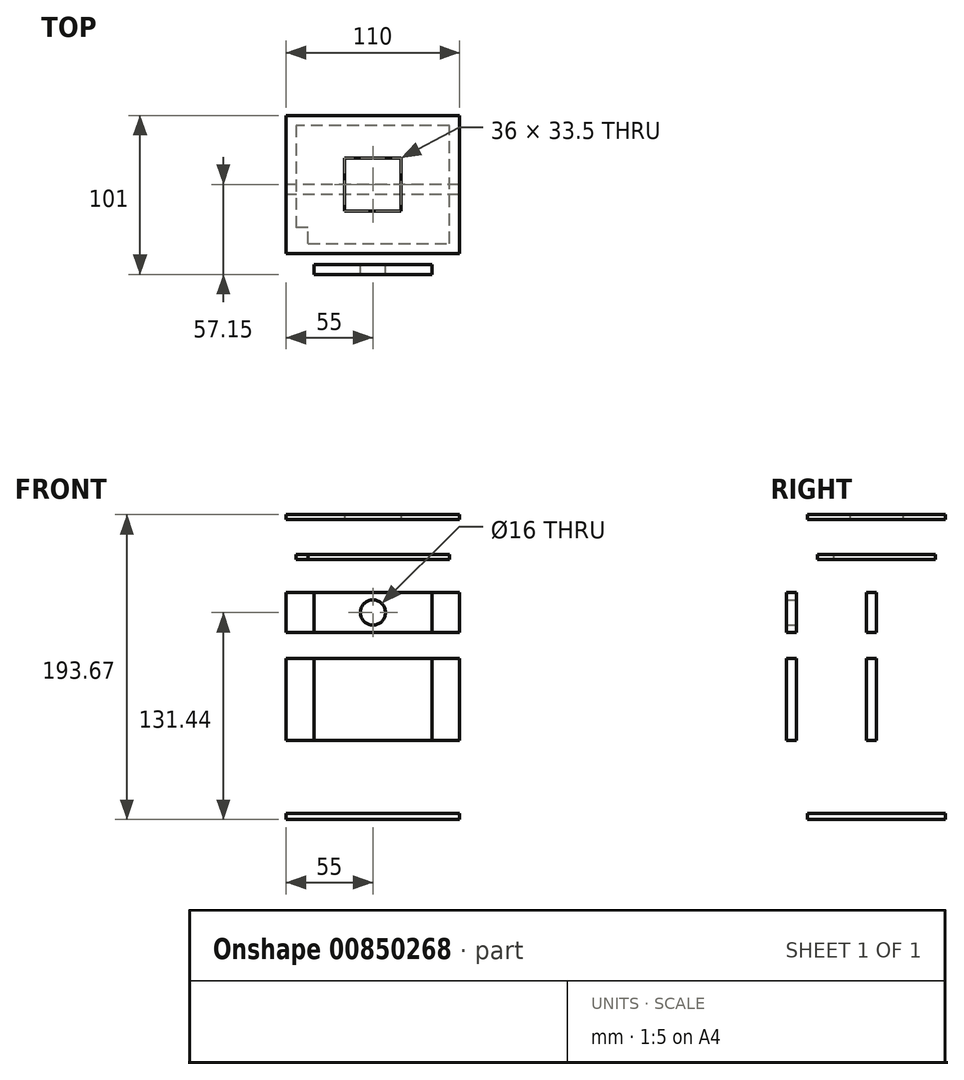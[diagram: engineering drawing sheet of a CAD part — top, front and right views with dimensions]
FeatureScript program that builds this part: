
annotation { "Feature Type Name" : "Feature", "Feature Type Description" : "" }
export const myFeature = defineFeature(function(context is Context, id is Id, definition is map)
    precondition{}
    {
        {
            var Q0;
            Q0=qCreatedBy(makeId("Front.planeOp"),FACE);
            var sketch = newSketch(context, id + "F0", { "sketchPlane" : qUnion([Q0])});
            skLineSegment(sketch, "E0.bottom", {"start": v(55, 26) * mm, "end": v(-55, 26) * mm});
            skLineSegment(sketch, "E0.top", {"start": v(55, -26) * mm, "end": v(-55, -26) * mm});
            skLineSegment(sketch, "E0.left", {"start": v(55, 26) * mm, "end": v(55, -26) * mm});
            skLineSegment(sketch, "E0.right", {"start": v(-55, 26) * mm, "end": v(-55, -26) * mm});
            skPoint(sketch, "E0.middle", {"position": v(0, 0) * mm});
            skSolve(sketch);
        }
        {
            var Q0;
            Q0=makeQuery(id+"F0.imprint","IMPRINT",FACE,{"disambiguationData":[TD([[makeQuery(id+"F0.imprint","IMPRINT",EDGE,{"derivedFrom":sQuery(id+"F0.wireOp",EDGE,"E0.bottom")}),1.0]])]});
            extrude(context, id + "F1", {"entities" : qUnion([Q0]), "depth" : 6.35 * mm, "offsetDistance" : 25.4 * mm});
        }
        {
            var Q0;
            Q0=qCreatedBy(makeId("Front.planeOp"),FACE);
            cPlane(context, id + "F2", {"entities" : qUnion([Q0]), "cplaneType" : CPlaneType.OFFSET, "offset" : 50.8 * mm, "width" : 152.4 * mm, "height" : 152.4 * mm});
        }
        {
            var Q0;
            Q0=qCreatedBy(id+"F2.planeOp",FACE);
            var sketch = newSketch(context, id + "F3", { "sketchPlane" : qUnion([Q0])});
            skLineSegment(sketch, "E1.bottom", {"start": v(37.5, 26) * mm, "end": v(-37.5, 26) * mm});
            skLineSegment(sketch, "E1.top", {"start": v(37.5, -26) * mm, "end": v(-37.5, -26) * mm});
            skLineSegment(sketch, "E1.left", {"start": v(37.5, 26) * mm, "end": v(37.5, -26) * mm});
            skLineSegment(sketch, "E1.right", {"start": v(-37.5, 26) * mm, "end": v(-37.5, -26) * mm});
            skPoint(sketch, "E1.middle", {"position": v(0, 0) * mm});
            skSolve(sketch);
        }
        {
            var Q0;
            Q0=makeQuery(id+"F3.imprint","IMPRINT",FACE,{"disambiguationData":[TD([[makeQuery(id+"F3.imprint","IMPRINT",EDGE,{"derivedFrom":sQuery(id+"F3.wireOp",EDGE,"E1.bottom")}),1.0]])]});
            extrude(context, id + "F4", {"entities" : qUnion([Q0]), "depth" : 6.35 * mm, "offsetDistance" : 25.4 * mm});
        }
        {
            var Q0;
            Q0=qCreatedBy(makeId("Top.planeOp"),FACE);
            cPlane(context, id + "F5", {"entities" : qUnion([Q0]), "cplaneType" : CPlaneType.OFFSET, "offset" : 76.2 * mm, "oppositeDirection" : true, "width" : 152.4 * mm, "height" : 152.4 * mm});
        }
        {
            var Q0;
            Q0=qCreatedBy(id+"F5.planeOp",FACE);
            var sketch = newSketch(context, id + "F6", { "sketchPlane" : qUnion([Q0])});
            skLineSegment(sketch, "E2.bottom", {"start": v(55, 43.85) * mm, "end": v(-55, 43.85) * mm});
            skLineSegment(sketch, "E2.top", {"start": v(55, -43.85) * mm, "end": v(-55, -43.85) * mm});
            skLineSegment(sketch, "E2.left", {"start": v(55, 43.85) * mm, "end": v(55, -43.85) * mm});
            skLineSegment(sketch, "E2.right", {"start": v(-55, 43.85) * mm, "end": v(-55, -43.85) * mm});
            skPoint(sketch, "E2.middle", {"position": v(0, 0) * mm});
            skSolve(sketch);
        }
        {
            var Q0;
            Q0=makeQuery(id+"F6.imprint","IMPRINT",FACE,{"disambiguationData":[TD([[makeQuery(id+"F6.imprint","IMPRINT",EDGE,{"derivedFrom":sQuery(id+"F6.wireOp",EDGE,"E2.bottom")}),1.0]])]});
            extrude(context, id + "F7", {"entities" : qUnion([Q0]), "depth" : 4 * mm, "offsetDistance" : 25.4 * mm});
        }
        {
            var Q0;
            Q0=qCreatedBy(makeId("Front.planeOp"),FACE);
            var sketch = newSketch(context, id + "F8", { "sketchPlane" : qUnion([Q0])});
            skLineSegment(sketch, "E3.bottom", {"start": v(55, 67.94) * mm, "end": v(-55, 67.94) * mm});
            skLineSegment(sketch, "E3.top", {"start": v(55, 42.54) * mm, "end": v(-55, 42.54) * mm});
            skLineSegment(sketch, "E3.left", {"start": v(55, 67.94) * mm, "end": v(55, 42.54) * mm});
            skLineSegment(sketch, "E3.right", {"start": v(-55, 67.94) * mm, "end": v(-55, 42.54) * mm});
            skPoint(sketch, "E3.middle", {"position": v(0, 55.24) * mm});
            skLineSegment(sketch, "E4.0.0", {"start": v(-55, -26) * mm, "end": v(55, -26) * mm});
            skLineSegment(sketch, "E4.0.1", {"start": v(55, -26) * mm, "end": v(55, 26) * mm});
            skLineSegment(sketch, "E4.0.2", {"start": v(55, 26) * mm, "end": v(-55, 26) * mm});
            skLineSegment(sketch, "E4.0.3", {"start": v(-55, 26) * mm, "end": v(-55, -26) * mm});
            skSolve(sketch);
        }
        {
            var Q0;
            Q0=makeQuery(id+"F8.imprint","IMPRINT",FACE,{"disambiguationData":[TD([[makeQuery(id+"F8.imprint","IMPRINT",EDGE,{"derivedFrom":sQuery(id+"F8.wireOp",EDGE,"E3.bottom")}),1.0]])]});
            extrude(context, id + "F9", {"entities" : qUnion([Q0]), "depth" : 6.35 * mm, "offsetDistance" : 25.4 * mm});
        }
        {
            var Q0;
            Q0=qCreatedBy(id+"F2.planeOp",FACE);
            var sketch = newSketch(context, id + "F10", { "sketchPlane" : qUnion([Q0])});
            skLineSegment(sketch, "E5.0.0", {"start": v(-37.5, -26) * mm, "end": v(37.5, -26) * mm});
            skLineSegment(sketch, "E5.0.1", {"start": v(37.5, -26) * mm, "end": v(37.5, 26) * mm});
            skLineSegment(sketch, "E5.0.2", {"start": v(37.5, 26) * mm, "end": v(-37.5, 26) * mm});
            skLineSegment(sketch, "E5.0.3", {"start": v(-37.5, 26) * mm, "end": v(-37.5, -26) * mm});
            skLineSegment(sketch, "E6.bottom", {"start": v(37.5, 67.94) * mm, "end": v(-37.5, 67.94) * mm});
            skLineSegment(sketch, "E6.top", {"start": v(37.5, 42.54) * mm, "end": v(-37.5, 42.54) * mm});
            skLineSegment(sketch, "E6.left", {"start": v(37.5, 67.94) * mm, "end": v(37.5, 42.54) * mm});
            skLineSegment(sketch, "E6.right", {"start": v(-37.5, 67.94) * mm, "end": v(-37.5, 42.54) * mm});
            skPoint(sketch, "E6.middle", {"position": v(0, 55.24) * mm});
            skLineSegment(sketch, "E7.0", {"start": v(55, 42.54) * mm, "end": v(-55, 42.54) * mm, "construction": true});
            skCircle(sketch, "E8", {"center": v(0, 55.24) * mm, "radius": 8 * mm});
            skSolve(sketch);
        }
        {
            var Q0;
            Q0=makeQuery(id+"F10.imprint","IMPRINT",FACE,{"disambiguationData":[TD([[makeQuery(id+"F10.imprint","IMPRINT",EDGE,{"derivedFrom":sQuery(id+"F10.wireOp",EDGE,"E6.bottom")}),1.0]])]});
            extrude(context, id + "F11", {"entities" : qUnion([Q0]), "depth" : 6.35 * mm, "offsetDistance" : 25.4 * mm});
        }
        {
            var Q0;
            Q0=qCreatedBy(id+"F5.planeOp",FACE);
            cPlane(context, id + "F12", {"entities" : qUnion([Q0]), "cplaneType" : CPlaneType.OFFSET, "offset" : 165.1 * mm, "width" : 152.4 * mm, "height" : 152.4 * mm});
        }
        {
            var Q0;
            Q0=qCreatedBy(id+"F12.planeOp",FACE);
            var sketch = newSketch(context, id + "F13", { "sketchPlane" : qUnion([Q0])});
            skLineSegment(sketch, "E9.0.0", {"start": v(-55, -43.85) * mm, "end": v(55, -43.85) * mm, "construction": true});
            skLineSegment(sketch, "E9.0.1", {"start": v(55, -43.85) * mm, "end": v(55, 43.85) * mm, "construction": true});
            skLineSegment(sketch, "E9.0.2", {"start": v(55, 43.85) * mm, "end": v(-55, 43.85) * mm, "construction": true});
            skLineSegment(sketch, "E9.0.3", {"start": v(-55, 43.85) * mm, "end": v(-55, -43.85) * mm, "construction": true});
            skLineSegment(sketch, "E10.0", {"start": v(48.65, 37.5) * mm, "end": v(-48.65, 37.5) * mm});
            skLineSegment(sketch, "E10.1", {"start": v(48.65, -37.5) * mm, "end": v(48.65, 37.5) * mm});
            skLineSegment(sketch, "E10.2", {"start": v(-48.65, -37.5) * mm, "end": v(48.65, -37.5) * mm});
            skLineSegment(sketch, "E10.3", {"start": v(-48.65, 37.5) * mm, "end": v(-48.65, -37.5) * mm});
            skLineSegment(sketch, "E11", {"start": v(-41.15, -37.5) * mm, "end": v(-41.15, -27.5) * mm});
            skLineSegment(sketch, "E12", {"start": v(-41.15, -27.5) * mm, "end": v(-48.65, -27.5) * mm});
            skSolve(sketch);
        }
        {
            var Q0;
            Q0=makeQuery(id+"F13.imprint","IMPRINT",FACE,{"disambiguationData":[TD([[makeQuery(id+"F13.imprint","IMPRINT",EDGE,{"derivedFrom":sQuery(id+"F13.wireOp",EDGE,"E10.0")}),1.0]])]});
            extrude(context, id + "F14", {"entities" : qUnion([Q0]), "depth" : 3.17 * mm, "offsetDistance" : 25.4 * mm});
        }
        {
            var Q0;
            Q0=qCreatedBy(id+"F12.planeOp",FACE);
            cPlane(context, id + "F15", {"entities" : qUnion([Q0]), "cplaneType" : CPlaneType.OFFSET, "offset" : 25.4 * mm, "width" : 152.4 * mm, "height" : 152.4 * mm});
        }
        {
            var Q0;
            Q0=qCreatedBy(id+"F15.planeOp",FACE);
            var sketch = newSketch(context, id + "F16", { "sketchPlane" : qUnion([Q0])});
            skLineSegment(sketch, "E13.0.0", {"start": v(-55, -43.85) * mm, "end": v(55, -43.85) * mm});
            skLineSegment(sketch, "E13.0.1", {"start": v(55, -43.85) * mm, "end": v(55, 43.85) * mm});
            skLineSegment(sketch, "E13.0.2", {"start": v(55, 43.85) * mm, "end": v(-55, 43.85) * mm});
            skLineSegment(sketch, "E13.0.3", {"start": v(-55, 43.85) * mm, "end": v(-55, -43.85) * mm});
            skLineSegment(sketch, "E14.bottom", {"start": v(18, 16.75) * mm, "end": v(-18, 16.75) * mm});
            skLineSegment(sketch, "E14.top", {"start": v(18, -16.75) * mm, "end": v(-18, -16.75) * mm});
            skLineSegment(sketch, "E14.left", {"start": v(18, 16.75) * mm, "end": v(18, -16.75) * mm});
            skLineSegment(sketch, "E14.right", {"start": v(-18, 16.75) * mm, "end": v(-18, -16.75) * mm});
            skPoint(sketch, "E14.middle", {"position": v(0, 0) * mm});
            skSolve(sketch);
        }
        {
            var Q0;
            Q0 = qSketchRegion(id + "F16", true);
            extrude(context, id + "F17", {"entities" : qUnion([Q0]), "depth" : 3.17 * mm, "offsetDistance" : 25.4 * mm});
        }
    });
